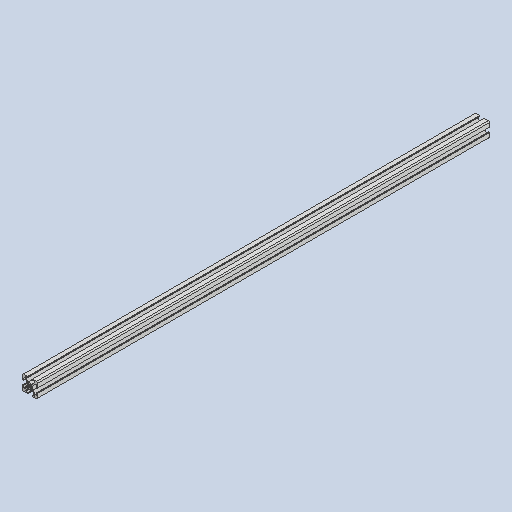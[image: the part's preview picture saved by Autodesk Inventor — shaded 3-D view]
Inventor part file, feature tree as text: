
AUTODESK INVENTOR PART (.ipt)
format: ipt  version: 2022 (Build 260153000, 153)  size: 280,576 bytes
history: native  units: in
note: dims shown in document units (in); Inventor stores cm internally (conversion verified against a paired STEP export)
features: other x3, plane x2, sketch x1
ambient origin geometry x8: Origin, YZ Plane, XZ Plane, XY Plane, X Axis, Y Axis, Z Axis, Center Point
bodies: Solid1 (feature_tree)
feature tree (6):
  other  "20x20x600 T Slot Extrusion Bar.ipt"
  other  "Solid1::20x20x600 T Slot Extrusion Bar.ipt"
  other  "TaggingFeature1"
  sketch  "Sketch_1"  dims[d0=0.3937in]
  plane  "Work Plane1"
  plane  "Work Plane2"
